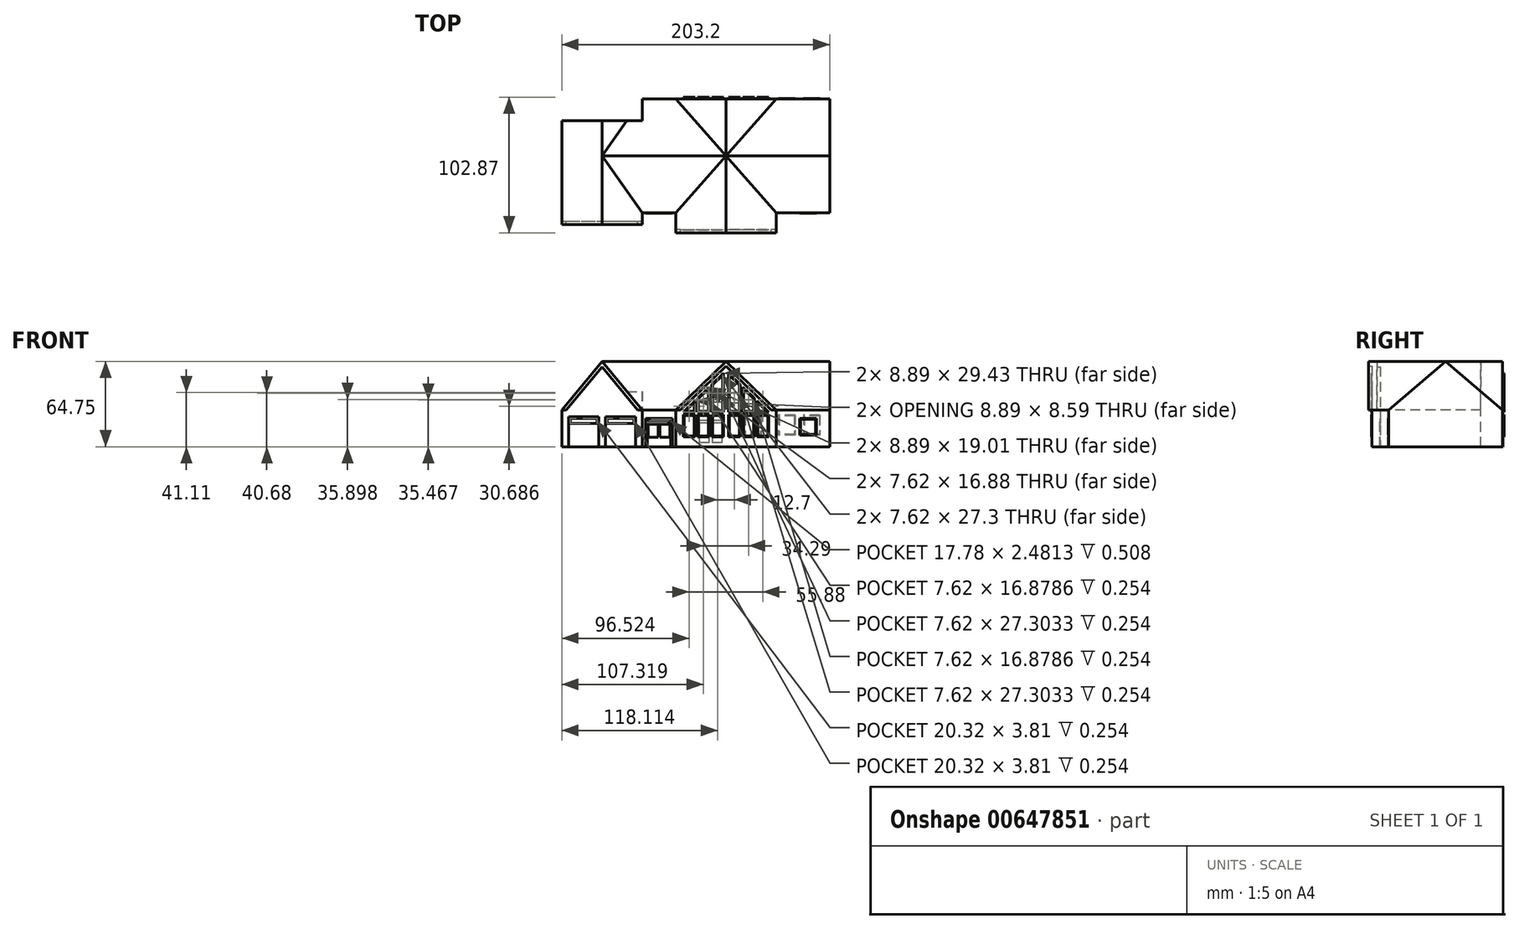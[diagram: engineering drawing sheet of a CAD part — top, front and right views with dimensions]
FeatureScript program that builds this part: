
annotation { "Feature Type Name" : "Feature", "Feature Type Description" : "" }
export const myFeature = defineFeature(function(context is Context, id is Id, definition is map)
    precondition{}
    {
        {
            var Q0;
            Q0=qCreatedBy(makeId("Front.planeOp"),FACE);
            var sketch = newSketch(context, id + "F0", { "sketchPlane" : qUnion([Q0])});
            skLineSegment(sketch, "E0", {"start": v(-75.74, -44.21) * mm, "end": v(66.5, -44.21) * mm});
            skLineSegment(sketch, "E1", {"start": v(66.5, -44.21) * mm, "end": v(66.5, -16.27) * mm});
            skLineSegment(sketch, "E2", {"start": v(66.5, -16.27) * mm, "end": v(-75.74, -16.27) * mm});
            skLineSegment(sketch, "E3", {"start": v(-75.74, -16.27) * mm, "end": v(-75.74, -44.21) * mm});
            skPoint(sketch, "E4", {"position": v(-50.34, -16.27) * mm});
            skPoint(sketch, "E5", {"position": v(25.86, -16.27) * mm});
            skLineSegment(sketch, "E6", {"start": v(-50.34, -16.27) * mm, "end": v(-12.24, 20.52) * mm});
            skLineSegment(sketch, "E7", {"start": v(-12.24, 20.52) * mm, "end": v(25.86, -16.27) * mm});
            skLineSegment(sketch, "E8.0", {"start": v(-12.24, 16.99) * mm, "end": v(22.2, -16.27) * mm});
            skLineSegment(sketch, "E8.1", {"start": v(-46.68, -16.27) * mm, "end": v(-12.24, 16.99) * mm});
            skSolve(sketch);
        }
        {
            var Q0;
            Q0=makeQuery(id+"F0.imprint","IMPRINT",FACE,{"disambiguationData":[TD([[makeQuery(id+"F0.imprint","IMPRINT",EDGE,{"derivedFrom":sQuery(id+"F0.wireOp",EDGE,"E0")}),1.0]])]});
            var Q1;
            {var subQ1=sQuery(id+"F0.wireOp",EDGE,"E6");Q1=makeQuery(id+"F0.imprint","IMPRINT",FACE,{"disambiguationData":[TD([[makeQuery(id+"F0.imprint","IMPRINT",EDGE,{"derivedFrom":subQ1}),-1.0]])]});}
            extrude(context, id + "F1", {"entities" : qUnion([Q0, Q1]), "oppositeDirection" : true, "depth" : 86.36 * mm, "offsetDistance" : 25.4 * mm});
        }
        {
            var Q0;
            {var subQ0=sQuery(id+"F0.wireOp",EDGE,"E8.0");Q0=makeQuery(id+"F0.imprint","IMPRINT",FACE,{"disambiguationData":[TD([[makeQuery(id+"F0.imprint","IMPRINT",EDGE,{"derivedFrom":subQ0}),-1.0]])]});}
            extrude(context, id + "F2", {"entities" : qUnion([Q0]), "operationType" : NewBodyOperationType.ADD, "oppositeDirection" : true, "depth" : 86.36 * mm, "offsetDistance" : 25.4 * mm});
        }
        {
            var Q0;
            Q0=makeQuery(id+"F1.opExtrude","SWEPT_FACE",FACE,{"disambiguationData":[OSD([sQuery(id+"F0.wireOp",EDGE,"E1")])]});
            var sketch = newSketch(context, id + "F3", { "sketchPlane" : qUnion([Q0])});
            skLineSegment(sketch, "E9", {"start": v(0, -16.27) * mm, "end": v(43.18, 20.54) * mm});
            skPoint(sketch, "E9.endSnap0", {"position": v(43.18, -16.27) * mm});
            skLineSegment(sketch, "E10", {"start": v(43.18, 20.54) * mm, "end": v(86.36, -16.27) * mm});
            skLineSegment(sketch, "E11", {"start": v(86.36, -16.27) * mm, "end": v(0, -16.27) * mm});
            skSolve(sketch);
        }
        {
            var Q0;
            Q0 = qSketchRegion(id + "F3", true);
            extrude(context, id + "F4", {"entities" : qUnion([Q0]), "operationType" : NewBodyOperationType.ADD, "oppositeDirection" : true, "depth" : 142.24 * mm, "offsetDistance" : 25.4 * mm});
        }
        {
            var Q0;
            {var subQ0=sQuery(id+"F0.wireOp",EDGE,"E8.1");var subQ1=sQuery(id+"F0.wireOp",EDGE,"E8.0");var subQ2=sQuery(id+"F0.wireOp",EDGE,"E2");Q0=makeQuery(id+"F2.boolean.opBoolean","MERGE",FACE,{"derivedFrom":[makeQuery(id+"F1.opExtrude","CAP_FACE",FACE,{"disambiguationData":[OSD([sQuery(id+"F0.wireOp",EDGE,"E0"),sQuery(id+"F0.wireOp",EDGE,"E1"),subQ2,sQuery(id+"F0.wireOp",EDGE,"E3"),sQuery(id+"F0.wireOp",EDGE,"E6"),sQuery(id+"F0.wireOp",EDGE,"E7"),subQ1,subQ0])],"isStart":true}),makeQuery(id+"F2.opExtrude","CAP_FACE",FACE,{"disambiguationData":[OSD([subQ2,subQ1,subQ0])],"isStart":true})]});}
            var sketch = newSketch(context, id + "F5", { "sketchPlane" : qUnion([Q0])});
            skLineSegment(sketch, "E12", {"start": v(-50.34, -16.27) * mm, "end": v(-50.34, -44.21) * mm});
            skLineSegment(sketch, "E13", {"start": v(-50.34, -44.21) * mm, "end": v(25.86, -44.21) * mm});
            skLineSegment(sketch, "E14", {"start": v(25.86, -44.21) * mm, "end": v(25.86, -16.27) * mm});
            skLineSegment(sketch, "E15", {"start": v(25.86, -16.27) * mm, "end": v(-50.34, -16.27) * mm});
            skSolve(sketch);
        }
        {
            var Q0;
            Q0=makeQuery(id+"F5.imprint","IMPRINT",FACE,{"disambiguationData":[TD([[makeQuery(id+"F5.imprint","IMPRINT",EDGE,{"derivedFrom":sQuery(id+"F5.wireOp",EDGE,"E12")}),1.0]])]});
            extrude(context, id + "F6", {"entities" : qUnion([Q0]), "operationType" : NewBodyOperationType.ADD, "depth" : 12.7 * mm, "offsetDistance" : 25.4 * mm});
        }
        {
            var Q0;
            {var subQ1=sQuery(id+"F0.wireOp",EDGE,"E6");Q0=makeQuery(id+"F0.imprint","IMPRINT",FACE,{"disambiguationData":[TD([[makeQuery(id+"F0.imprint","IMPRINT",EDGE,{"derivedFrom":subQ1}),-1.0]])]});}
            extrude(context, id + "F7", {"entities" : qUnion([Q0]), "operationType" : NewBodyOperationType.ADD, "depth" : 15.24 * mm, "offsetDistance" : 25.4 * mm});
        }
        {
            var Q0;
            {var subQ0=sQuery(id+"F0.wireOp",EDGE,"E8.0");Q0=makeQuery(id+"F0.imprint","IMPRINT",FACE,{"disambiguationData":[TD([[makeQuery(id+"F0.imprint","IMPRINT",EDGE,{"derivedFrom":subQ0}),-1.0]])]});}
            extrude(context, id + "F8", {"entities" : qUnion([Q0]), "operationType" : NewBodyOperationType.ADD, "depth" : 12.7 * mm, "offsetDistance" : 25.4 * mm});
        }
        {
            var Q0;
            {var subQ0=sQuery(id+"F0.wireOp",EDGE,"E6");var subQ1=sQuery(id+"F0.wireOp",EDGE,"E3");var subQ2=sQuery(id+"F0.wireOp",EDGE,"E8.1");var subQ3=sQuery(id+"F0.wireOp",EDGE,"E8.0");var subQ4=sQuery(id+"F0.wireOp",EDGE,"E2");var subQ5=sQuery(id+"F0.wireOp",EDGE,"E0");var subQ6=makeQuery(id+"F1.opExtrude","CAP_FACE",FACE,{"disambiguationData":[OSD([subQ5,sQuery(id+"F0.wireOp",EDGE,"E1"),subQ4,subQ1,subQ0,sQuery(id+"F0.wireOp",EDGE,"E7"),subQ3,subQ2])],"isStart":true});var subQ7=sQuery(id+"F3.wireOp",EDGE,"E9");var subQ8=makeQuery(id+"F2.opExtrude","CAP_FACE",FACE,{"disambiguationData":[OSD([subQ4,subQ3,subQ2])],"isStart":true});Q0=makeQuery(id+"F6.boolean.opBoolean","SPLIT",FACE,{"disambiguationData":[TD([makeQuery(id+"F1.opExtrude","SWEPT_FACE",FACE,{"disambiguationData":[OSD([subQ5])]}),subQ6,makeQuery(id+"F1.opExtrude","SWEPT_FACE",FACE,{"disambiguationData":[OSD([subQ1])]}),makeQuery(id+"F1.opExtrude","SWEPT_FACE",FACE,{"disambiguationData":[OSD([subQ0])]}),subQ8,makeQuery(id+"F4.opExtrude","SWEPT_FACE",FACE,{"disambiguationData":[OSD([subQ7])]}),makeQuery(id+"F4.opExtrude","CAP_FACE",FACE,{"disambiguationData":[OSD([subQ7,sQuery(id+"F3.wireOp",EDGE,"E10"),sQuery(id+"F3.wireOp",EDGE,"E11")])],"isStart":false}),makeQuery(id+"F6.opExtrude","SWEPT_FACE",FACE,{"disambiguationData":[OSD([sQuery(id+"F5.wireOp",EDGE,"E12")])]}),makeQuery(id+"F6.opExtrude","SWEPT_FACE",FACE,{"disambiguationData":[OSD([sQuery(id+"F5.wireOp",EDGE,"E13")])]}),makeQuery(id+"F6.opExtrude","SWEPT_FACE",FACE,{"disambiguationData":[OSD([sQuery(id+"F5.wireOp",EDGE,"E15")])]})])],"derivedFrom":makeQuery(id+"F2.boolean.opBoolean","MERGE",FACE,{"derivedFrom":[subQ6,subQ8]})});}
            var sketch = newSketch(context, id + "F9", { "sketchPlane" : qUnion([Q0])});
            skLineSegment(sketch, "E16", {"start": v(-73.2, -44.21) * mm, "end": v(-73.2, -22.62) * mm});
            skLineSegment(sketch, "E17", {"start": v(-73.2, -22.62) * mm, "end": v(-52.88, -22.62) * mm});
            skLineSegment(sketch, "E18", {"start": v(-52.88, -22.62) * mm, "end": v(-52.88, -44.21) * mm});
            skLineSegment(sketch, "E19", {"start": v(-52.88, -44.21) * mm, "end": v(-73.2, -44.21) * mm});
            skLineSegment(sketch, "E20.0", {"start": v(-52.84, -22.59) * mm, "end": v(-52.84, -44.21) * mm});
            skLineSegment(sketch, "E20.1", {"start": v(-73.23, -22.59) * mm, "end": v(-52.84, -22.59) * mm});
            skLineSegment(sketch, "E20.2", {"start": v(-73.23, -44.21) * mm, "end": v(-73.23, -22.59) * mm});
            skLineSegment(sketch, "E21.0", {"start": v(-54.18, -26.43) * mm, "end": v(-54.18, -44.21) * mm});
            skLineSegment(sketch, "E21.2", {"start": v(-71.96, -44.21) * mm, "end": v(-71.96, -26.43) * mm});
            skLineSegment(sketch, "E22", {"start": v(-71.96, -26.43) * mm, "end": v(-54.18, -26.43) * mm});
            skLineSegment(sketch, "E23.bottom", {"start": v(-71.96, -23.25) * mm, "end": v(-54.18, -23.25) * mm});
            skLineSegment(sketch, "E23.top", {"start": v(-71.96, -25.73) * mm, "end": v(-54.18, -25.73) * mm});
            skLineSegment(sketch, "E23.left", {"start": v(-71.96, -23.25) * mm, "end": v(-71.96, -25.73) * mm});
            skLineSegment(sketch, "E23.right", {"start": v(-54.18, -23.25) * mm, "end": v(-54.18, -25.73) * mm});
            skLineSegment(sketch, "E24", {"start": v(-63.07, -26.43) * mm, "end": v(-63.07, -44.21) * mm});
            skLineSegment(sketch, "E25.bottom", {"start": v(-62.44, -27.27) * mm, "end": v(-54.82, -27.27) * mm});
            skLineSegment(sketch, "E25.top", {"start": v(-62.44, -37.11) * mm, "end": v(-54.82, -37.11) * mm});
            skLineSegment(sketch, "E25.left", {"start": v(-62.44, -27.27) * mm, "end": v(-62.44, -37.11) * mm});
            skLineSegment(sketch, "E25.right", {"start": v(-54.82, -27.27) * mm, "end": v(-54.82, -37.11) * mm});
            skLineSegment(sketch, "E26.bottom", {"start": v(-63.7, -27.27) * mm, "end": v(-71.33, -27.27) * mm});
            skLineSegment(sketch, "E26.top", {"start": v(-63.7, -37.11) * mm, "end": v(-71.33, -37.11) * mm});
            skLineSegment(sketch, "E26.left", {"start": v(-63.7, -27.27) * mm, "end": v(-63.7, -37.11) * mm});
            skLineSegment(sketch, "E26.right", {"start": v(-71.33, -27.27) * mm, "end": v(-71.33, -37.11) * mm});
            skSolve(sketch);
        }
        {
            var Q0;
            {var subQ2=sQuery(id+"F9.wireOp",EDGE,"E21.2");Q0=makeQuery(id+"F9.imprint","IMPRINT",FACE,{"disambiguationData":[TD([[makeQuery(id+"F9.imprint","IMPRINT",EDGE,{"derivedFrom":subQ2}),-1.0]])]});}
            var Q1;
            {var subQ2=sQuery(id+"F9.wireOp",EDGE,"E21.0");Q1=makeQuery(id+"F9.imprint","IMPRINT",FACE,{"disambiguationData":[TD([[makeQuery(id+"F9.imprint","IMPRINT",EDGE,{"derivedFrom":subQ2}),-1.0]])]});}
            extrude(context, id + "F10", {"entities" : qUnion([Q0, Q1]), "operationType" : NewBodyOperationType.ADD, "depth" : 0.25 * mm, "offsetDistance" : 25.4 * mm});
        }
        {
            var Q0;
            {var subQ10=sQuery(id+"F9.wireOp",EDGE,"E16");Q0=makeQuery(id+"F9.imprint","IMPRINT",FACE,{"disambiguationData":[TD([[makeQuery(id+"F9.imprint","IMPRINT",EDGE,{"derivedFrom":subQ10}),-1.0]])]});}
            extrude(context, id + "F11", {"entities" : qUnion([Q0]), "operationType" : NewBodyOperationType.ADD, "depth" : 0.5 * mm, "offsetDistance" : 25.4 * mm});
        }
        {
            var Q0;
            Q0=makeQuery(id+"F8.boolean.opBoolean","MERGE",FACE,{"derivedFrom":[makeQuery(id+"F6.opExtrude","CAP_FACE",FACE,{"disambiguationData":[OSD([sQuery(id+"F5.wireOp",EDGE,"E12"),sQuery(id+"F5.wireOp",EDGE,"E13"),sQuery(id+"F5.wireOp",EDGE,"E14"),sQuery(id+"F5.wireOp",EDGE,"E15")])],"isStart":false}),makeQuery(id+"F8.opExtrude","CAP_FACE",FACE,{"disambiguationData":[OSD([sQuery(id+"F0.wireOp",EDGE,"E2"),sQuery(id+"F0.wireOp",EDGE,"E8.0"),sQuery(id+"F0.wireOp",EDGE,"E8.1")])],"isStart":false})]});
            var sketch = newSketch(context, id + "F12", { "sketchPlane" : qUnion([Q0])});
            skPoint(sketch, "E27", {"position": v(-14.14, 11.62) * mm});
            skPoint(sketch, "E28", {"position": v(-23.03, 3.03) * mm});
            skPoint(sketch, "E29", {"position": v(-24.94, 1.2) * mm});
            skPoint(sketch, "E30", {"position": v(-33.83, -7.4) * mm});
            skPoint(sketch, "E31", {"position": v(-35.73, -9.23) * mm});
            skPoint(sketch, "E32", {"position": v(-44.62, -17.82) * mm});
            skLineSegment(sketch, "E33", {"start": v(-44.62, -17.82) * mm, "end": v(-35.73, -17.82) * mm});
            skLineSegment(sketch, "E34", {"start": v(-35.73, -17.82) * mm, "end": v(-35.73, -9.23) * mm});
            skLineSegment(sketch, "E35", {"start": v(-44.62, -17.82) * mm, "end": v(-35.73, -9.23) * mm});
            skLineSegment(sketch, "E36", {"start": v(-24.94, 1.2) * mm, "end": v(-33.83, -7.4) * mm});
            skLineSegment(sketch, "E37", {"start": v(-33.83, -17.82) * mm, "end": v(-33.83, -7.4) * mm});
            skLineSegment(sketch, "E38", {"start": v(-33.83, -17.82) * mm, "end": v(-24.94, -17.82) * mm});
            skLineSegment(sketch, "E39", {"start": v(-24.94, -17.82) * mm, "end": v(-24.94, 1.2) * mm});
            skLineSegment(sketch, "E40", {"start": v(-23.03, 3.03) * mm, "end": v(-23.03, -17.82) * mm});
            skLineSegment(sketch, "E41", {"start": v(-23.03, -17.82) * mm, "end": v(-14.14, -17.82) * mm});
            skLineSegment(sketch, "E42", {"start": v(-14.14, -17.82) * mm, "end": v(-14.14, 11.62) * mm});
            skLineSegment(sketch, "E43", {"start": v(-12.24, 16.99) * mm, "end": v(-12.24, -44.21) * mm, "construction": true});
            skLineSegment(sketch, "E44", {"start": v(-44.62, -19.72) * mm, "end": v(-44.62, -36.6) * mm});
            skLineSegment(sketch, "E45", {"start": v(-44.62, -36.6) * mm, "end": v(-35.73, -36.6) * mm});
            skLineSegment(sketch, "E46", {"start": v(-35.73, -36.6) * mm, "end": v(-35.73, -19.72) * mm});
            skLineSegment(sketch, "E47", {"start": v(-35.73, -19.72) * mm, "end": v(-44.62, -19.72) * mm});
            skLineSegment(sketch, "E48", {"start": v(-33.83, -19.72) * mm, "end": v(-24.94, -19.72) * mm});
            skLineSegment(sketch, "E49", {"start": v(-24.94, -19.72) * mm, "end": v(-24.94, -36.6) * mm});
            skLineSegment(sketch, "E50", {"start": v(-24.94, -36.6) * mm, "end": v(-33.83, -36.6) * mm});
            skLineSegment(sketch, "E51", {"start": v(-33.83, -36.6) * mm, "end": v(-33.83, -19.72) * mm});
            skLineSegment(sketch, "E52", {"start": v(-23.03, -19.72) * mm, "end": v(-14.14, -19.72) * mm});
            skLineSegment(sketch, "E53", {"start": v(-14.14, -19.72) * mm, "end": v(-14.14, -36.6) * mm});
            skLineSegment(sketch, "E54", {"start": v(-14.14, -36.6) * mm, "end": v(-23.03, -36.6) * mm});
            skLineSegment(sketch, "E55", {"start": v(-23.03, -36.6) * mm, "end": v(-23.03, -19.72) * mm});
            skLineSegment(sketch, "E56", {"start": v(-23.03, 3.03) * mm, "end": v(-14.14, 11.62) * mm});
            skLineSegment(sketch, "E57.0", {"start": v(-56.69, -9.92) * mm, "end": v(-56.69, -50.56) * mm});
            skLineSegment(sketch, "E57.1", {"start": v(-49.24, -9.92) * mm, "end": v(-56.69, -9.92) * mm});
            skLineSegment(sketch, "E57.2", {"start": v(32.21, -50.56) * mm, "end": v(32.21, -9.92) * mm});
            skLineSegment(sketch, "E57.3", {"start": v(32.21, -9.92) * mm, "end": v(24.77, -9.92) * mm});
            skLineSegment(sketch, "E57.4", {"start": v(24.77, -9.92) * mm, "end": v(-12.24, 25.82) * mm});
            skLineSegment(sketch, "E57.5", {"start": v(-56.69, -50.56) * mm, "end": v(32.21, -50.56) * mm});
            skLineSegment(sketch, "E57.6", {"start": v(-12.24, 25.82) * mm, "end": v(-49.24, -9.92) * mm});
            skLineSegment(sketch, "E58.0", {"start": v(-22.4, 2.76) * mm, "end": v(-14.78, 10.12) * mm});
            skLineSegment(sketch, "E58.1", {"start": v(-22.4, 2.76) * mm, "end": v(-22.4, -17.18) * mm});
            skLineSegment(sketch, "E59.0", {"start": v(-14.78, -17.18) * mm, "end": v(-14.78, 10.12) * mm});
            skLineSegment(sketch, "E59.1", {"start": v(-22.4, -17.18) * mm, "end": v(-14.78, -17.18) * mm});
            skLineSegment(sketch, "E60.0", {"start": v(-25.57, -17.18) * mm, "end": v(-25.57, -0.3) * mm});
            skLineSegment(sketch, "E60.1", {"start": v(-33.2, -17.18) * mm, "end": v(-25.57, -17.18) * mm});
            skLineSegment(sketch, "E61.0", {"start": v(-33.2, -17.18) * mm, "end": v(-33.2, -7.66) * mm});
            skLineSegment(sketch, "E62.trimOffspring", {"start": v(-25.57, -0.3) * mm, "end": v(-33.2, -7.66) * mm});
            skLineSegment(sketch, "E63.0", {"start": v(-36.37, -17.18) * mm, "end": v(-36.37, -10.73) * mm});
            skLineSegment(sketch, "E63.1", {"start": v(-43.05, -17.18) * mm, "end": v(-36.37, -17.18) * mm});
            skLineSegment(sketch, "E64.trimOffspring", {"start": v(-43.05, -17.18) * mm, "end": v(-36.37, -10.73) * mm});
            skLineSegment(sketch, "E65.0", {"start": v(-22.4, -20.36) * mm, "end": v(-14.78, -20.36) * mm});
            skLineSegment(sketch, "E65.1", {"start": v(-22.4, -35.96) * mm, "end": v(-22.4, -20.36) * mm});
            skLineSegment(sketch, "E65.2", {"start": v(-14.78, -35.96) * mm, "end": v(-22.4, -35.96) * mm});
            skLineSegment(sketch, "E66.0", {"start": v(-14.78, -20.36) * mm, "end": v(-14.78, -35.96) * mm});
            skLineSegment(sketch, "E67.0", {"start": v(-33.2, -20.36) * mm, "end": v(-25.57, -20.36) * mm});
            skLineSegment(sketch, "E67.1", {"start": v(-33.2, -35.96) * mm, "end": v(-33.2, -20.36) * mm});
            skLineSegment(sketch, "E67.2", {"start": v(-25.57, -35.96) * mm, "end": v(-33.2, -35.96) * mm});
            skLineSegment(sketch, "E68.0", {"start": v(-25.57, -20.36) * mm, "end": v(-25.57, -35.96) * mm});
            skLineSegment(sketch, "E69.0", {"start": v(-43.99, -35.96) * mm, "end": v(-36.37, -35.96) * mm});
            skLineSegment(sketch, "E69.1", {"start": v(-43.99, -20.36) * mm, "end": v(-43.99, -35.96) * mm});
            skLineSegment(sketch, "E69.2", {"start": v(-36.37, -20.36) * mm, "end": v(-43.99, -20.36) * mm});
            skLineSegment(sketch, "E70.0", {"start": v(-36.37, -35.96) * mm, "end": v(-36.37, -20.36) * mm});
            skLineSegment(sketch, "E71.MirrorCS", {"start": v(8.72, -20.36) * mm, "end": v(1.1, -20.36) * mm});
            skLineSegment(sketch, "E72.MirrorCS", {"start": v(11.26, -17.82) * mm, "end": v(11.26, -9.23) * mm});
            skLineSegment(sketch, "E73.MirrorCS", {"start": v(11.9, -17.18) * mm, "end": v(11.9, -10.73) * mm});
            skLineSegment(sketch, "E74.MirrorCS", {"start": v(11.26, -19.72) * mm, "end": v(20.15, -19.72) * mm});
            skLineSegment(sketch, "E75.MirrorCS", {"start": v(-2.08, -20.36) * mm, "end": v(-9.7, -20.36) * mm});
            skLineSegment(sketch, "E76.MirrorCS", {"start": v(-1.44, -19.72) * mm, "end": v(-10.33, -19.72) * mm});
            skLineSegment(sketch, "E77.MirrorCS", {"start": v(11.9, -20.36) * mm, "end": v(19.51, -20.36) * mm});
            skLineSegment(sketch, "E78.MirrorCS", {"start": v(9.35, -19.72) * mm, "end": v(0.46, -19.72) * mm});
            skLineSegment(sketch, "E79.MirrorCS", {"start": v(11.9, -35.96) * mm, "end": v(11.9, -20.36) * mm});
            skLineSegment(sketch, "E80.MirrorCS", {"start": v(8.72, -17.18) * mm, "end": v(8.72, -7.66) * mm});
            skLineSegment(sketch, "E81.MirrorCS", {"start": v(-10.33, -36.6) * mm, "end": v(-1.44, -36.6) * mm});
            skLineSegment(sketch, "E82.MirrorCS", {"start": v(20.15, -17.82) * mm, "end": v(11.26, -17.82) * mm});
            skPoint(sketch, "E83.MirrorP", {"position": v(-10.33, 11.62) * mm});
            skLineSegment(sketch, "E84.MirrorCS", {"start": v(20.15, -17.82) * mm, "end": v(11.26, -9.23) * mm});
            skPoint(sketch, "E85.MirrorP", {"position": v(11.26, -9.23) * mm});
            skLineSegment(sketch, "E86.MirrorCS", {"start": v(-2.08, -35.96) * mm, "end": v(-2.08, -20.36) * mm});
            skLineSegment(sketch, "E87.MirrorCS", {"start": v(-1.44, 3.03) * mm, "end": v(-10.33, 11.62) * mm});
            skLineSegment(sketch, "E88.MirrorCS", {"start": v(11.26, -36.6) * mm, "end": v(11.26, -19.72) * mm});
            skLineSegment(sketch, "E89.MirrorCS", {"start": v(9.35, -17.82) * mm, "end": v(0.46, -17.82) * mm});
            skLineSegment(sketch, "E90.MirrorCS", {"start": v(-12.24, 25.82) * mm, "end": v(24.77, -9.92) * mm});
            skLineSegment(sketch, "E91.MirrorCS", {"start": v(-2.08, 2.76) * mm, "end": v(-2.08, -17.18) * mm});
            skLineSegment(sketch, "E92.MirrorCS", {"start": v(0.46, -19.72) * mm, "end": v(0.46, -36.6) * mm});
            skLineSegment(sketch, "E93.MirrorCS", {"start": v(1.1, -35.96) * mm, "end": v(8.72, -35.96) * mm});
            skLineSegment(sketch, "E94.MirrorCS", {"start": v(-10.33, -19.72) * mm, "end": v(-10.33, -36.6) * mm});
            skLineSegment(sketch, "E95.MirrorCS", {"start": v(1.1, -17.18) * mm, "end": v(1.1, -0.3) * mm});
            skLineSegment(sketch, "E96.MirrorCS", {"start": v(18.58, -17.18) * mm, "end": v(11.9, -10.73) * mm});
            skLineSegment(sketch, "E97.MirrorCS", {"start": v(-2.08, -17.18) * mm, "end": v(-9.7, -17.18) * mm});
            skLineSegment(sketch, "E98.MirrorCS", {"start": v(1.1, -20.36) * mm, "end": v(1.1, -35.96) * mm});
            skLineSegment(sketch, "E99.MirrorCS", {"start": v(19.51, -20.36) * mm, "end": v(19.51, -35.96) * mm});
            skLineSegment(sketch, "E100.MirrorCS", {"start": v(-9.7, -20.36) * mm, "end": v(-9.7, -35.96) * mm});
            skLineSegment(sketch, "E101.MirrorCS", {"start": v(0.46, -17.82) * mm, "end": v(0.46, 1.2) * mm});
            skLineSegment(sketch, "E102.MirrorCS", {"start": v(0.46, 1.2) * mm, "end": v(9.35, -7.4) * mm});
            skPoint(sketch, "E103.MirrorP", {"position": v(0.46, 1.2) * mm});
            skLineSegment(sketch, "E104.MirrorCS", {"start": v(-10.33, -17.82) * mm, "end": v(-10.33, 11.62) * mm});
            skLineSegment(sketch, "E105.MirrorCS", {"start": v(-9.7, -35.96) * mm, "end": v(-2.08, -35.96) * mm});
            skLineSegment(sketch, "E106.MirrorCS", {"start": v(19.51, -35.96) * mm, "end": v(11.9, -35.96) * mm});
            skLineSegment(sketch, "E107.MirrorCS", {"start": v(-1.44, 3.03) * mm, "end": v(-1.44, -17.82) * mm});
            skPoint(sketch, "E108.MirrorP", {"position": v(20.15, -17.82) * mm});
            skLineSegment(sketch, "E109.MirrorCS", {"start": v(-9.7, -17.18) * mm, "end": v(-9.7, 10.12) * mm});
            skLineSegment(sketch, "E110.MirrorCS", {"start": v(9.35, -17.82) * mm, "end": v(9.35, -7.4) * mm});
            skLineSegment(sketch, "E111.MirrorCS", {"start": v(20.15, -19.72) * mm, "end": v(20.15, -36.6) * mm});
            skLineSegment(sketch, "E112.MirrorCS", {"start": v(18.58, -17.18) * mm, "end": v(11.9, -17.18) * mm});
            skLineSegment(sketch, "E113.MirrorCS", {"start": v(-1.44, -17.82) * mm, "end": v(-10.33, -17.82) * mm});
            skLineSegment(sketch, "E114.MirrorCS", {"start": v(-1.44, -36.6) * mm, "end": v(-1.44, -19.72) * mm});
            skLineSegment(sketch, "E115.MirrorCS", {"start": v(1.1, -0.3) * mm, "end": v(8.72, -7.66) * mm});
            skLineSegment(sketch, "E116.MirrorCS", {"start": v(20.15, -36.6) * mm, "end": v(11.26, -36.6) * mm});
            skLineSegment(sketch, "E117.MirrorCS", {"start": v(8.72, -17.18) * mm, "end": v(1.1, -17.18) * mm});
            skPoint(sketch, "E118.MirrorP", {"position": v(9.35, -7.4) * mm});
            skLineSegment(sketch, "E119.MirrorCS", {"start": v(8.72, -35.96) * mm, "end": v(8.72, -20.36) * mm});
            skLineSegment(sketch, "E120.MirrorCS", {"start": v(9.35, -36.6) * mm, "end": v(9.35, -19.72) * mm});
            skLineSegment(sketch, "E121.MirrorCS", {"start": v(0.46, -36.6) * mm, "end": v(9.35, -36.6) * mm});
            skLineSegment(sketch, "E122.MirrorCS", {"start": v(-2.08, 2.76) * mm, "end": v(-9.7, 10.12) * mm});
            skPoint(sketch, "E123.MirrorP", {"position": v(-1.44, 3.03) * mm});
            skSolve(sketch);
        }
        {
            var Q0;
            Q0=makeQuery(id+"F12.imprint","IMPRINT",FACE,{"disambiguationData":[TD([[makeQuery(id+"F12.imprint","IMPRINT",EDGE,{"derivedFrom":sQuery(id+"F12.wireOp",EDGE,"E74.MirrorCS")}),-1.0]])]});
            var Q1;
            Q1=makeQuery(id+"F12.imprint","IMPRINT",FACE,{"disambiguationData":[TD([[makeQuery(id+"F12.imprint","IMPRINT",EDGE,{"derivedFrom":sQuery(id+"F12.wireOp",EDGE,"E71.MirrorCS")}),-1.0]])]});
            var Q2;
            Q2=makeQuery(id+"F12.imprint","IMPRINT",FACE,{"disambiguationData":[TD([[makeQuery(id+"F12.imprint","IMPRINT",EDGE,{"derivedFrom":sQuery(id+"F12.wireOp",EDGE,"E72.MirrorCS")}),-1.0]])]});
            var Q3;
            Q3=makeQuery(id+"F12.imprint","IMPRINT",FACE,{"disambiguationData":[TD([[makeQuery(id+"F12.imprint","IMPRINT",EDGE,{"derivedFrom":sQuery(id+"F12.wireOp",EDGE,"E80.MirrorCS")}),-1.0]])]});
            var Q4;
            Q4=makeQuery(id+"F12.imprint","IMPRINT",FACE,{"disambiguationData":[TD([[makeQuery(id+"F12.imprint","IMPRINT",EDGE,{"derivedFrom":sQuery(id+"F12.wireOp",EDGE,"E87.MirrorCS")}),1.0]])]});
            var Q5;
            Q5=makeQuery(id+"F12.imprint","IMPRINT",FACE,{"disambiguationData":[TD([[makeQuery(id+"F12.imprint","IMPRINT",EDGE,{"derivedFrom":sQuery(id+"F12.wireOp",EDGE,"E40")}),1.0]])]});
            var Q6;
            Q6=makeQuery(id+"F12.imprint","IMPRINT",FACE,{"disambiguationData":[TD([[makeQuery(id+"F12.imprint","IMPRINT",EDGE,{"derivedFrom":sQuery(id+"F12.wireOp",EDGE,"E36")}),1.0]])]});
            var Q7;
            Q7=makeQuery(id+"F12.imprint","IMPRINT",FACE,{"disambiguationData":[TD([[makeQuery(id+"F12.imprint","IMPRINT",EDGE,{"derivedFrom":sQuery(id+"F12.wireOp",EDGE,"E75.MirrorCS")}),-1.0]])]});
            var Q8;
            Q8=makeQuery(id+"F12.imprint","IMPRINT",FACE,{"disambiguationData":[TD([[makeQuery(id+"F12.imprint","IMPRINT",EDGE,{"derivedFrom":sQuery(id+"F12.wireOp",EDGE,"E52")}),-1.0]])]});
            var Q9;
            Q9=makeQuery(id+"F12.imprint","IMPRINT",FACE,{"disambiguationData":[TD([[makeQuery(id+"F12.imprint","IMPRINT",EDGE,{"derivedFrom":sQuery(id+"F12.wireOp",EDGE,"E44")}),1.0]])]});
            var Q10;
            Q10=makeQuery(id+"F12.imprint","IMPRINT",FACE,{"disambiguationData":[TD([[makeQuery(id+"F12.imprint","IMPRINT",EDGE,{"derivedFrom":sQuery(id+"F12.wireOp",EDGE,"E48")}),-1.0]])]});
            var Q11;
            Q11=makeQuery(id+"F12.imprint","IMPRINT",FACE,{"disambiguationData":[TD([[makeQuery(id+"F12.imprint","IMPRINT",EDGE,{"derivedFrom":sQuery(id+"F12.wireOp",EDGE,"E33")}),1.0]])]});
            extrude(context, id + "F13", {"entities" : qUnion([Q0, Q1, Q2, Q3, Q4, Q5, Q6, Q7, Q8, Q9, Q10, Q11]), "operationType" : NewBodyOperationType.ADD, "depth" : 0.25 * mm, "offsetDistance" : 25.4 * mm});
        }
        {
            var Q0;
            Q0=makeQuery(id+"F12.imprint","IMPRINT",FACE,{"disambiguationData":[TD([[makeQuery(id+"F12.imprint","IMPRINT",EDGE,{"derivedFrom":sQuery(id+"F12.wireOp",EDGE,"E44")}),1.0]])]});
            var Q1;
            Q1=makeQuery(id+"F12.imprint","IMPRINT",FACE,{"disambiguationData":[TD([[makeQuery(id+"F12.imprint","IMPRINT",EDGE,{"derivedFrom":sQuery(id+"F12.wireOp",EDGE,"E40")}),1.0]])]});
            var Q2;
            Q2=makeQuery(id+"F12.imprint","IMPRINT",FACE,{"disambiguationData":[TD([[makeQuery(id+"F12.imprint","IMPRINT",EDGE,{"derivedFrom":sQuery(id+"F12.wireOp",EDGE,"E36")}),1.0]])]});
            var Q3;
            Q3=makeQuery(id+"F12.imprint","IMPRINT",FACE,{"disambiguationData":[TD([[makeQuery(id+"F12.imprint","IMPRINT",EDGE,{"derivedFrom":sQuery(id+"F12.wireOp",EDGE,"E87.MirrorCS")}),1.0]])]});
            var Q4;
            Q4=makeQuery(id+"F12.imprint","IMPRINT",FACE,{"disambiguationData":[TD([[makeQuery(id+"F12.imprint","IMPRINT",EDGE,{"derivedFrom":sQuery(id+"F12.wireOp",EDGE,"E33")}),1.0]])]});
            var Q5;
            Q5=makeQuery(id+"F12.imprint","IMPRINT",FACE,{"disambiguationData":[TD([[makeQuery(id+"F12.imprint","IMPRINT",EDGE,{"derivedFrom":sQuery(id+"F12.wireOp",EDGE,"E80.MirrorCS")}),-1.0]])]});
            var Q6;
            Q6=makeQuery(id+"F12.imprint","IMPRINT",FACE,{"disambiguationData":[TD([[makeQuery(id+"F12.imprint","IMPRINT",EDGE,{"derivedFrom":sQuery(id+"F12.wireOp",EDGE,"E72.MirrorCS")}),-1.0]])]});
            extrude(context, id + "F14", {"entities" : qUnion([Q0, Q1, Q2, Q3, Q4, Q5, Q6]), "operationType" : NewBodyOperationType.ADD, "oppositeDirection" : true, "depth" : 100.33 * mm, "offsetDistance" : 25.4 * mm});
        }
        {
            var Q0;
            {var subQ1=sQuery(id+"F0.wireOp",EDGE,"E8.1");var subQ2=sQuery(id+"F0.wireOp",EDGE,"E8.0");var subQ3=sQuery(id+"F0.wireOp",EDGE,"E2");var subQ4=sQuery(id+"F0.wireOp",EDGE,"E3");var subQ6=sQuery(id+"F0.wireOp",EDGE,"E7");var subQ7=sQuery(id+"F0.wireOp",EDGE,"E6");var subQ8=sQuery(id+"F0.wireOp",EDGE,"E1");var subQ9=sQuery(id+"F0.wireOp",EDGE,"E0");var subQ10=makeQuery(id+"F1.opExtrude","SWEPT_FACE",FACE,{"disambiguationData":[OSD([subQ9])]});Q0=makeQuery(id+"F14.boolean.opBoolean","SPLIT",FACE,{"disambiguationData":[TD([subQ10])],"derivedFrom":makeQuery(id+"F2.boolean.opBoolean","MERGE",FACE,{"derivedFrom":[makeQuery(id+"F1.opExtrude","CAP_FACE",FACE,{"disambiguationData":[OSD([subQ9,subQ8,subQ3,subQ4,subQ7,subQ6,subQ2,subQ1])],"isStart":false}),makeQuery(id+"F2.opExtrude","CAP_FACE",FACE,{"disambiguationData":[OSD([subQ3,subQ2,subQ1])],"isStart":false})]})});}
            var sketch = newSketch(context, id + "F15", { "sketchPlane" : qUnion([Q0])});
            skLineSegment(sketch, "E124", {"start": v(14.14, -19.86) * mm, "end": v(33.83, -19.86) * mm});
            skLineSegment(sketch, "E125", {"start": v(14.14, -44.21) * mm, "end": v(14.14, -19.86) * mm});
            skLineSegment(sketch, "E126", {"start": v(33.83, -19.86) * mm, "end": v(33.83, -44.21) * mm});
            skLineSegment(sketch, "E127.bottom", {"start": v(14.78, -20.5) * mm, "end": v(33.2, -20.5) * mm});
            skLineSegment(sketch, "E127.top", {"start": v(14.78, -24.3) * mm, "end": v(33.2, -24.3) * mm});
            skLineSegment(sketch, "E127.left", {"start": v(14.78, -20.5) * mm, "end": v(14.78, -24.3) * mm});
            skLineSegment(sketch, "E127.right", {"start": v(33.2, -20.5) * mm, "end": v(33.2, -24.3) * mm});
            skLineSegment(sketch, "E128.0", {"start": v(52.9, -9.92) * mm, "end": v(12.24, 29.35) * mm});
            skLineSegment(sketch, "E128.1", {"start": v(82.09, -9.92) * mm, "end": v(52.9, -9.92) * mm});
            skLineSegment(sketch, "E128.2", {"start": v(-28.43, -9.92) * mm, "end": v(-72.85, -9.92) * mm});
            skLineSegment(sketch, "E128.3", {"start": v(-72.85, -9.92) * mm, "end": v(-72.85, -50.56) * mm});
            skLineSegment(sketch, "E128.4", {"start": v(-72.85, -50.56) * mm, "end": v(82.09, -50.56) * mm});
            skLineSegment(sketch, "E128.5", {"start": v(12.24, 29.35) * mm, "end": v(-28.43, -9.92) * mm});
            skLineSegment(sketch, "E128.6", {"start": v(82.09, -50.56) * mm, "end": v(82.09, -9.92) * mm});
            skLineSegment(sketch, "E129.bottom", {"start": v(15.41, -26.21) * mm, "end": v(22.71, -26.21) * mm});
            skLineSegment(sketch, "E129.top", {"start": v(15.41, -41.18) * mm, "end": v(22.71, -41.18) * mm});
            skLineSegment(sketch, "E129.left", {"start": v(15.41, -26.21) * mm, "end": v(15.41, -41.18) * mm});
            skLineSegment(sketch, "E129.right", {"start": v(22.71, -26.21) * mm, "end": v(22.71, -41.18) * mm});
            skLineSegment(sketch, "E130.bottom", {"start": v(25.25, -26.21) * mm, "end": v(32.56, -26.21) * mm});
            skLineSegment(sketch, "E130.top", {"start": v(25.25, -41.18) * mm, "end": v(32.56, -41.18) * mm});
            skLineSegment(sketch, "E130.left", {"start": v(25.25, -26.21) * mm, "end": v(25.25, -41.18) * mm});
            skLineSegment(sketch, "E130.right", {"start": v(32.56, -26.21) * mm, "end": v(32.56, -41.18) * mm});
            skSolve(sketch);
        }
        {
            var Q0;
            Q0=makeQuery(id+"F15.imprint","IMPRINT",FACE,{"disambiguationData":[TD([[makeQuery(id+"F15.imprint","IMPRINT",EDGE,{"derivedFrom":sQuery(id+"F15.wireOp",EDGE,"E124")}),-1.0]])]});
            extrude(context, id + "F16", {"entities" : qUnion([Q0]), "operationType" : NewBodyOperationType.ADD, "depth" : 0.25 * mm, "offsetDistance" : 25.4 * mm});
        }
        {
            var Q0;
            Q0=makeQuery(id+"F4.boolean.opBoolean","MERGE",FACE,{"derivedFrom":[makeQuery(id+"F1.opExtrude","SWEPT_FACE",FACE,{"disambiguationData":[OSD([sQuery(id+"F0.wireOp",EDGE,"E3")])]}),makeQuery(id+"F4.opExtrude","CAP_FACE",FACE,{"disambiguationData":[OSD([sQuery(id+"F3.wireOp",EDGE,"E9"),sQuery(id+"F3.wireOp",EDGE,"E10"),sQuery(id+"F3.wireOp",EDGE,"E11")])],"isStart":false})]});
            var sketch = newSketch(context, id + "F17", { "sketchPlane" : qUnion([Q0])});
            skLineSegment(sketch, "E131", {"start": v(-69.94, -44.21) * mm, "end": v(6.26, -44.21) * mm});
            skLineSegment(sketch, "E132", {"start": v(-69.94, -44.21) * mm, "end": v(-69.94, -16.27) * mm});
            skLineSegment(sketch, "E133", {"start": v(-69.94, -16.27) * mm, "end": v(6.26, -16.27) * mm});
            skLineSegment(sketch, "E134", {"start": v(6.26, -16.27) * mm, "end": v(6.26, -44.21) * mm});
            skLineSegment(sketch, "E135", {"start": v(-69.94, -16.27) * mm, "end": v(-69.94, -2.28) * mm});
            skLineSegment(sketch, "E136", {"start": v(-69.94, -2.28) * mm, "end": v(-43.18, 20.54) * mm});
            skLineSegment(sketch, "E137", {"start": v(-43.18, 20.54) * mm, "end": v(0, -16.27) * mm});
            skLineSegment(sketch, "E138", {"start": v(0, -16.27) * mm, "end": v(-69.94, -16.27) * mm});
            skSolve(sketch);
        }
        {
            var Q0;
            {var subQ3=sQuery(id+"F17.wireOp",EDGE,"E134");Q0=makeQuery(id+"F17.imprint","IMPRINT",FACE,{"disambiguationData":[TD([[makeQuery(id+"F17.imprint","IMPRINT",EDGE,{"derivedFrom":subQ3}),-1.0]])]});}
            var Q1;
            {var subQ4=sQuery(id+"F17.wireOp",EDGE,"E132");Q1=makeQuery(id+"F17.imprint","IMPRINT",FACE,{"disambiguationData":[TD([[makeQuery(id+"F17.imprint","IMPRINT",EDGE,{"derivedFrom":subQ4}),-1.0]])]});}
            extrude(context, id + "F18", {"entities" : qUnion([Q0, Q1]), "operationType" : NewBodyOperationType.ADD, "depth" : 60.96 * mm, "offsetDistance" : 25.4 * mm});
        }
        {
            var Q0;
            Q0=makeQuery(id+"F18.opExtrude","SWEPT_FACE",FACE,{"disambiguationData":[OSD([sQuery(id+"F17.wireOp",EDGE,"E134")])]});
            var sketch = newSketch(context, id + "F19", { "sketchPlane" : qUnion([Q0])});
            skLineSegment(sketch, "E139", {"start": v(-136.7, -16.27) * mm, "end": v(-106.22, 20.52) * mm});
            skPoint(sketch, "E139.endSnap0", {"position": v(-106.22, -16.27) * mm});
            skLineSegment(sketch, "E140", {"start": v(-106.22, 20.52) * mm, "end": v(-75.74, -16.27) * mm});
            skLineSegment(sketch, "E141", {"start": v(-136.7, -16.27) * mm, "end": v(-75.74, -16.27) * mm});
            skLineSegment(sketch, "E142.0", {"start": v(-106.22, 16.54) * mm, "end": v(-79.03, -16.27) * mm});
            skLineSegment(sketch, "E142.1", {"start": v(-133.4, -16.27) * mm, "end": v(-106.22, 16.54) * mm});
            skSolve(sketch);
        }
        {
            var Q0;
            {var subQ4=sQuery(id+"F19.wireOp",EDGE,"E139");Q0=makeQuery(id+"F19.imprint","IMPRINT",FACE,{"disambiguationData":[TD([[makeQuery(id+"F19.imprint","IMPRINT",EDGE,{"derivedFrom":subQ4}),-1.0]])]});}
            var Q1;
            {var subQ0=sQuery(id+"F19.wireOp",EDGE,"E142.0");Q1=makeQuery(id+"F19.imprint","IMPRINT",FACE,{"disambiguationData":[TD([[makeQuery(id+"F19.imprint","IMPRINT",EDGE,{"derivedFrom":subQ0}),-1.0]])]});}
            extrude(context, id + "F20", {"entities" : qUnion([Q0, Q1]), "operationType" : NewBodyOperationType.ADD, "oppositeDirection" : true, "depth" : 76.2 * mm, "offsetDistance" : 25.4 * mm});
        }
        {
            var Q0;
            {var subQ4=sQuery(id+"F19.wireOp",EDGE,"E139");Q0=makeQuery(id+"F19.imprint","IMPRINT",FACE,{"disambiguationData":[TD([[makeQuery(id+"F19.imprint","IMPRINT",EDGE,{"derivedFrom":subQ4}),-1.0]])]});}
            extrude(context, id + "F21", {"entities" : qUnion([Q0]), "operationType" : NewBodyOperationType.ADD, "depth" : 2.54 * mm, "offsetDistance" : 25.4 * mm});
        }
        {
            var Q0;
            Q0=makeQuery(id+"F17.imprint","IMPRINT",FACE,{"disambiguationData":[TD([[makeQuery(id+"F17.imprint","IMPRINT",EDGE,{"derivedFrom":sQuery(id+"F17.wireOp",EDGE,"E135")}),-1.0]])]});
            extrude(context, id + "F22", {"entities" : qUnion([Q0]), "operationType" : NewBodyOperationType.ADD, "depth" : 30.48 * mm, "offsetDistance" : 25.4 * mm});
        }
        {
            var Q0;
            Q0=makeQuery(id+"F20.boolean.opBoolean","MERGE",FACE,{"derivedFrom":[makeQuery(id+"F18.opExtrude","SWEPT_FACE",FACE,{"disambiguationData":[OSD([sQuery(id+"F17.wireOp",EDGE,"E134")])]}),makeQuery(id+"F20.opExtrude","CAP_FACE",FACE,{"disambiguationData":[OSD([sQuery(id+"F19.wireOp",EDGE,"E139"),sQuery(id+"F19.wireOp",EDGE,"E140"),sQuery(id+"F19.wireOp",EDGE,"E141")])],"isStart":true})]});
            var sketch = newSketch(context, id + "F23", { "sketchPlane" : qUnion([Q0])});
            skLineSegment(sketch, "E143", {"start": v(-131.62, -44.21) * mm, "end": v(-131.62, -21.35) * mm});
            skLineSegment(sketch, "E144", {"start": v(-131.62, -21.35) * mm, "end": v(-108.76, -21.35) * mm});
            skLineSegment(sketch, "E145", {"start": v(-108.76, -21.35) * mm, "end": v(-108.76, -44.21) * mm});
            skLineSegment(sketch, "E146", {"start": v(-108.76, -44.21) * mm, "end": v(-131.62, -44.21) * mm});
            skLineSegment(sketch, "E147", {"start": v(-103.68, -44.21) * mm, "end": v(-103.68, -21.35) * mm});
            skLineSegment(sketch, "E148", {"start": v(-103.68, -21.35) * mm, "end": v(-80.82, -21.35) * mm});
            skLineSegment(sketch, "E149", {"start": v(-80.82, -21.35) * mm, "end": v(-80.82, -44.21) * mm});
            skLineSegment(sketch, "E150", {"start": v(-80.82, -44.21) * mm, "end": v(-103.68, -44.21) * mm});
            skLineSegment(sketch, "E151.bottom", {"start": v(-130.35, -22.62) * mm, "end": v(-110.03, -22.62) * mm});
            skLineSegment(sketch, "E151.top", {"start": v(-130.35, -26.43) * mm, "end": v(-110.03, -26.43) * mm});
            skLineSegment(sketch, "E151.left", {"start": v(-130.35, -22.62) * mm, "end": v(-130.35, -26.43) * mm});
            skLineSegment(sketch, "E151.right", {"start": v(-110.03, -22.62) * mm, "end": v(-110.03, -26.43) * mm});
            skLineSegment(sketch, "E152.bottom", {"start": v(-102.43, -22.62) * mm, "end": v(-82.1, -22.62) * mm});
            skLineSegment(sketch, "E152.top", {"start": v(-102.43, -26.43) * mm, "end": v(-82.1, -26.43) * mm});
            skLineSegment(sketch, "E152.left", {"start": v(-102.43, -22.62) * mm, "end": v(-102.43, -26.43) * mm});
            skLineSegment(sketch, "E152.right", {"start": v(-82.1, -22.62) * mm, "end": v(-82.1, -26.43) * mm});
            skSolve(sketch);
        }
        {
            var Q0;
            Q0=makeQuery(id+"F23.imprint","IMPRINT",FACE,{"disambiguationData":[TD([[makeQuery(id+"F23.imprint","IMPRINT",EDGE,{"derivedFrom":sQuery(id+"F23.wireOp",EDGE,"E147")}),-1.0]])]});
            var Q1;
            Q1=makeQuery(id+"F23.imprint","IMPRINT",FACE,{"disambiguationData":[TD([[makeQuery(id+"F23.imprint","IMPRINT",EDGE,{"derivedFrom":sQuery(id+"F23.wireOp",EDGE,"E143")}),-1.0]])]});
            extrude(context, id + "F24", {"entities" : qUnion([Q0, Q1]), "operationType" : NewBodyOperationType.ADD, "depth" : 0.25 * mm, "offsetDistance" : 25.4 * mm});
        }
        {
            var Q0;
            {var subQ14=sQuery(id+"F0.wireOp",EDGE,"E8.1");var subQ15=sQuery(id+"F0.wireOp",EDGE,"E8.0");var subQ16=sQuery(id+"F0.wireOp",EDGE,"E2");var subQ17=sQuery(id+"F0.wireOp",EDGE,"E3");var subQ19=sQuery(id+"F0.wireOp",EDGE,"E7");var subQ20=sQuery(id+"F0.wireOp",EDGE,"E6");var subQ21=sQuery(id+"F0.wireOp",EDGE,"E1");var subQ22=sQuery(id+"F0.wireOp",EDGE,"E0");var subQ23=makeQuery(id+"F1.opExtrude","SWEPT_FACE",FACE,{"disambiguationData":[OSD([subQ22])]});Q0=makeQuery(id+"F16.boolean.opBoolean","SPLIT",FACE,{"disambiguationData":[TD([subQ23])],"derivedFrom":makeQuery(id+"F14.boolean.opBoolean","SPLIT",FACE,{"disambiguationData":[TD([subQ23])],"derivedFrom":makeQuery(id+"F2.boolean.opBoolean","MERGE",FACE,{"derivedFrom":[makeQuery(id+"F1.opExtrude","CAP_FACE",FACE,{"disambiguationData":[OSD([subQ22,subQ21,subQ16,subQ17,subQ20,subQ19,subQ15,subQ14])],"isStart":false}),makeQuery(id+"F2.opExtrude","CAP_FACE",FACE,{"disambiguationData":[OSD([subQ16,subQ15,subQ14])],"isStart":false})]})})});}
            var sketch = newSketch(context, id + "F25", { "sketchPlane" : qUnion([Q0])});
            skLineSegment(sketch, "E153.bottom", {"start": v(-59.13, -20.1) * mm, "end": v(-46.43, -20.1) * mm});
            skLineSegment(sketch, "E153.top", {"start": v(-59.13, -35.32) * mm, "end": v(-46.43, -35.32) * mm});
            skLineSegment(sketch, "E153.left", {"start": v(-59.13, -20.1) * mm, "end": v(-59.13, -35.32) * mm});
            skLineSegment(sketch, "E153.right", {"start": v(-46.43, -20.1) * mm, "end": v(-46.43, -35.32) * mm});
            skLineSegment(sketch, "E154.0", {"start": v(-58.5, -20.73) * mm, "end": v(-47.07, -20.73) * mm});
            skLineSegment(sketch, "E154.1", {"start": v(-58.5, -20.73) * mm, "end": v(-58.5, -34.69) * mm});
            skLineSegment(sketch, "E154.2", {"start": v(-58.5, -34.69) * mm, "end": v(-47.07, -34.69) * mm});
            skLineSegment(sketch, "E154.3", {"start": v(-47.07, -20.73) * mm, "end": v(-47.07, -34.69) * mm});
            skLineSegment(sketch, "E155.bottom", {"start": v(-40.27, -20.1) * mm, "end": v(-27.57, -20.1) * mm});
            skLineSegment(sketch, "E155.top", {"start": v(-40.27, -35.32) * mm, "end": v(-27.57, -35.32) * mm});
            skLineSegment(sketch, "E155.left", {"start": v(-40.27, -20.1) * mm, "end": v(-40.27, -35.32) * mm});
            skLineSegment(sketch, "E155.right", {"start": v(-27.57, -20.1) * mm, "end": v(-27.57, -35.32) * mm});
            skLineSegment(sketch, "E156.0", {"start": v(-39.64, -20.73) * mm, "end": v(-28.2, -20.73) * mm});
            skLineSegment(sketch, "E156.1", {"start": v(-39.64, -20.73) * mm, "end": v(-39.64, -34.69) * mm});
            skLineSegment(sketch, "E156.2", {"start": v(-39.64, -34.69) * mm, "end": v(-28.2, -34.69) * mm});
            skLineSegment(sketch, "E156.3", {"start": v(-28.2, -20.73) * mm, "end": v(-28.2, -34.69) * mm});
            skLineSegment(sketch, "E157.bottom", {"start": v(-14.53, -20.1) * mm, "end": v(-1.83, -20.1) * mm});
            skLineSegment(sketch, "E157.top", {"start": v(-14.53, -35.32) * mm, "end": v(-1.83, -35.32) * mm});
            skLineSegment(sketch, "E157.left", {"start": v(-14.53, -20.1) * mm, "end": v(-14.53, -35.32) * mm});
            skLineSegment(sketch, "E157.right", {"start": v(-1.83, -20.1) * mm, "end": v(-1.83, -35.32) * mm});
            skLineSegment(sketch, "E158.0", {"start": v(-13.9, -20.73) * mm, "end": v(-2.46, -20.73) * mm});
            skLineSegment(sketch, "E158.1", {"start": v(-13.9, -20.73) * mm, "end": v(-13.9, -34.69) * mm});
            skLineSegment(sketch, "E158.2", {"start": v(-13.9, -34.69) * mm, "end": v(-2.46, -34.69) * mm});
            skLineSegment(sketch, "E158.3", {"start": v(-2.46, -20.73) * mm, "end": v(-2.46, -34.69) * mm});
            skSolve(sketch);
        }
        {
            var Q0;
            Q0=makeQuery(id+"F25.imprint","IMPRINT",FACE,{"disambiguationData":[TD([[makeQuery(id+"F25.imprint","IMPRINT",EDGE,{"derivedFrom":sQuery(id+"F25.wireOp",EDGE,"E153.bottom")}),-1.0]])]});
            var Q1;
            Q1=makeQuery(id+"F25.imprint","IMPRINT",FACE,{"disambiguationData":[TD([[makeQuery(id+"F25.imprint","IMPRINT",EDGE,{"derivedFrom":sQuery(id+"F25.wireOp",EDGE,"E155.bottom")}),-1.0]])]});
            var Q2;
            Q2=makeQuery(id+"F25.imprint","IMPRINT",FACE,{"disambiguationData":[TD([[makeQuery(id+"F25.imprint","IMPRINT",EDGE,{"derivedFrom":sQuery(id+"F25.wireOp",EDGE,"E157.bottom")}),-1.0]])]});
            extrude(context, id + "F26", {"entities" : qUnion([Q0, Q1, Q2]), "operationType" : NewBodyOperationType.ADD, "depth" : 0.25 * mm, "offsetDistance" : 25.4 * mm});
        }
        {
            var Q0;
            {var subQ0=sQuery(id+"F0.wireOp",EDGE,"E7");var subQ1=sQuery(id+"F3.wireOp",EDGE,"E9");var subQ2=sQuery(id+"F0.wireOp",EDGE,"E1");var subQ3=sQuery(id+"F0.wireOp",EDGE,"E8.1");var subQ4=sQuery(id+"F0.wireOp",EDGE,"E8.0");var subQ5=sQuery(id+"F0.wireOp",EDGE,"E2");var subQ6=sQuery(id+"F0.wireOp",EDGE,"E0");var subQ7=makeQuery(id+"F1.opExtrude","CAP_FACE",FACE,{"disambiguationData":[OSD([subQ6,subQ2,subQ5,sQuery(id+"F0.wireOp",EDGE,"E3"),sQuery(id+"F0.wireOp",EDGE,"E6"),subQ0,subQ4,subQ3])],"isStart":true});var subQ8=makeQuery(id+"F2.opExtrude","CAP_FACE",FACE,{"disambiguationData":[OSD([subQ5,subQ4,subQ3])],"isStart":true});Q0=makeQuery(id+"F6.boolean.opBoolean","SPLIT",FACE,{"disambiguationData":[TD([makeQuery(id+"F1.opExtrude","SWEPT_FACE",FACE,{"disambiguationData":[OSD([subQ6])]}),subQ7,makeQuery(id+"F1.opExtrude","SWEPT_FACE",FACE,{"disambiguationData":[OSD([subQ2])]}),makeQuery(id+"F1.opExtrude","SWEPT_FACE",FACE,{"disambiguationData":[OSD([subQ0])]}),subQ8,makeQuery(id+"F4.opExtrude","SWEPT_FACE",FACE,{"disambiguationData":[OSD([subQ1])]}),makeQuery(id+"F4.opExtrude","CAP_FACE",FACE,{"disambiguationData":[OSD([subQ1,sQuery(id+"F3.wireOp",EDGE,"E10"),sQuery(id+"F3.wireOp",EDGE,"E11")])],"isStart":true}),makeQuery(id+"F6.opExtrude","SWEPT_FACE",FACE,{"disambiguationData":[OSD([sQuery(id+"F5.wireOp",EDGE,"E13")])]}),makeQuery(id+"F6.opExtrude","SWEPT_FACE",FACE,{"disambiguationData":[OSD([sQuery(id+"F5.wireOp",EDGE,"E14")])]}),makeQuery(id+"F6.opExtrude","SWEPT_FACE",FACE,{"disambiguationData":[OSD([sQuery(id+"F5.wireOp",EDGE,"E15")])]})])],"derivedFrom":makeQuery(id+"F2.boolean.opBoolean","MERGE",FACE,{"derivedFrom":[subQ7,subQ8]})});}
            var sketch = newSketch(context, id + "F27", { "sketchPlane" : qUnion([Q0])});
            skLineSegment(sketch, "E159.bottom", {"start": v(43.76, -22.62) * mm, "end": v(56.46, -22.62) * mm});
            skLineSegment(sketch, "E159.top", {"start": v(43.76, -35.32) * mm, "end": v(56.46, -35.32) * mm});
            skLineSegment(sketch, "E159.left", {"start": v(43.76, -22.62) * mm, "end": v(43.76, -35.32) * mm});
            skLineSegment(sketch, "E159.right", {"start": v(56.46, -22.62) * mm, "end": v(56.46, -35.32) * mm});
            skLineSegment(sketch, "E160.0", {"start": v(44.4, -23.26) * mm, "end": v(55.82, -23.26) * mm});
            skLineSegment(sketch, "E160.1", {"start": v(44.4, -23.26) * mm, "end": v(44.4, -34.69) * mm});
            skLineSegment(sketch, "E160.2", {"start": v(44.4, -34.69) * mm, "end": v(55.82, -34.69) * mm});
            skLineSegment(sketch, "E160.3", {"start": v(55.82, -23.26) * mm, "end": v(55.82, -34.69) * mm});
            skSolve(sketch);
        }
        {
            var Q0;
            Q0=makeQuery(id+"F27.imprint","IMPRINT",FACE,{"disambiguationData":[TD([[makeQuery(id+"F27.imprint","IMPRINT",EDGE,{"derivedFrom":sQuery(id+"F27.wireOp",EDGE,"E159.bottom")}),-1.0]])]});
            extrude(context, id + "F28", {"entities" : qUnion([Q0]), "operationType" : NewBodyOperationType.ADD, "depth" : 0.25 * mm, "offsetDistance" : 25.4 * mm});
        }
    });
